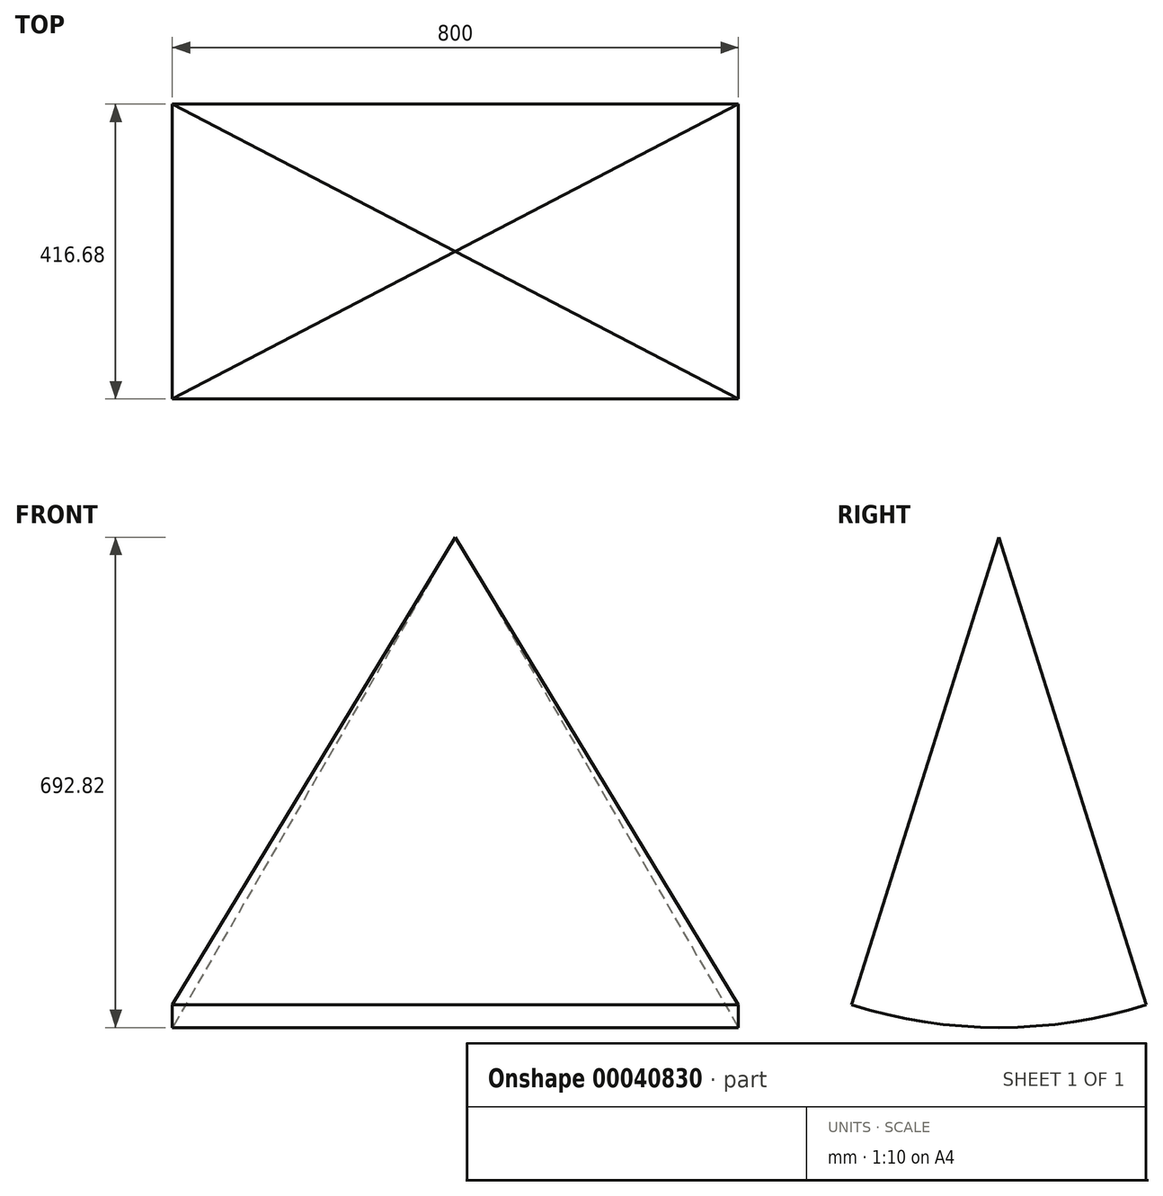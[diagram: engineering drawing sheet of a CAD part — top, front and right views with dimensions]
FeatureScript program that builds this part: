
annotation { "Feature Type Name" : "Feature", "Feature Type Description" : "" }
export const myFeature = defineFeature(function(context is Context, id is Id, definition is map)
    precondition{}
    {
        {
            var Q0;
            Q0=qCreatedBy(makeId("Front.planeOp"),FACE);
            var sketch = newSketch(context, id + "F0", { "sketchPlane" : qUnion([Q0])});
            skLineSegment(sketch, "E0", {"start": v(0, 359.44) * mm, "end": v(-400, -333.38) * mm});
            skLineSegment(sketch, "E1", {"start": v(-400, -333.38) * mm, "end": v(0, -333.38) * mm});
            skLineSegment(sketch, "E2", {"start": v(0, -333.38) * mm, "end": v(0, 359.44) * mm});
            skLineSegment(sketch, "E3", {"start": v(0, 359.44) * mm, "end": v(-568.45, 359.44) * mm, "construction": true});
            skSolve(sketch);
        }
        {
            var Q0;
            Q0=makeQuery(id+"F0.imprint","IMPRINT",FACE,{"disambiguationData":[TD([[makeQuery(id+"F0.imprint","IMPRINT",EDGE,{"derivedFrom":sQuery(id+"F0.wireOp",EDGE,"E0")}),1.0]])]});
            var Q1;
            Q1=sQuery(id+"F0.wireOp",EDGE,"E3");
            revolve(context, id + "F1", {"entities" : qUnion([Q0]), "axis" : qUnion([Q1]), "revolveType" : RevolveType.SYMMETRIC, "oppositeDirection" : true, "angle" : 35 * degree});
        }
        {
            var Q0;
            Q0=makeQuery(id+"F1.opRevolve","SWEPT_BODY",BODY,{"disambiguationData":[OSD([sQuery(id+"F0.wireOp",EDGE,"E0"),sQuery(id+"F0.wireOp",EDGE,"E1"),sQuery(id+"F0.wireOp",EDGE,"E2")])]});
            var Q1;
            Q1=makeQuery(id+"F1.opRevolve","SWEPT_FACE",FACE,{"disambiguationData":[OSD([sQuery(id+"F0.wireOp",EDGE,"E2")])]});
            mirror(context, id + "F2", {"operationType" : NewBodyOperationType.ADD, "entities" : qUnion([Q0]), "mirrorPlane" : qUnion([Q1])});
        }
    });
